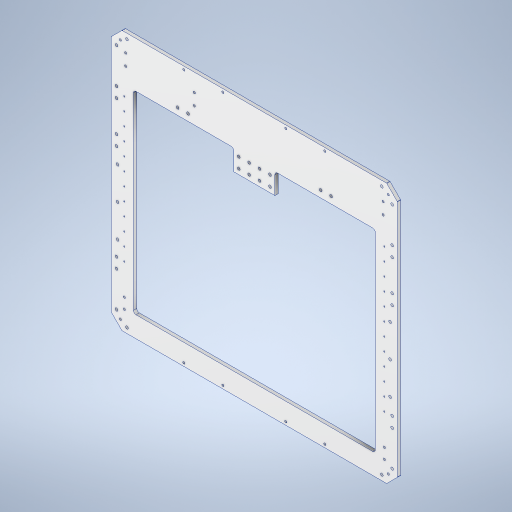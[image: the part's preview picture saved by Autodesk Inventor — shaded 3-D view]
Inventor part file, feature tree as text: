
AUTODESK INVENTOR PART (.ipt)
format: ipt  version: 2024 (Build 280153000, 153)  size: 780,800 bytes
history: native  units: mm
features: sketch x10, hole x6, extrude x4, projected_geometry x4, fillet x3, mirror x2
ambient origin geometry x8: Origin, YZ Plane, XZ Plane, XY Plane, X Axis, Y Axis, Z Axis, Center Point
bodies: Solid1 (feature_tree)
feature tree (29):
  extrude  "Extrusion1"  Depth=500.0mm
  hole  "Hole1"  [1 undecoded]
  extrude  "Extrusion4"  Depth=40.0mm
  extrude  "Extrusion5"  Depth=40.0mm
  hole  "Hole6"  [1 undecoded]
  hole  "Hole7"  [1 undecoded]
  mirror  "Mirror1"
  hole  "Hole8"  [1 undecoded]
  fillet  "Fillet2"  Radius=40.0mm
  fillet  "Fillet3"  Radius=20.0mm
  fillet  "Fillet4"  Radius=40.0mm
  extrude  "Extrusion6"  Depth=40.0mm
  hole  "Hole9"  [1 undecoded]
  hole  "Hole10"  [1 undecoded]
  mirror  "Mirror2"
  sketch  "Sketch1"  dims[d0=550.0mm d1=500.0mm]
  sketch  "Sketch2"  dims[d2=6.35mm d3=0.0mm d4=40.0mm]
  sketch  "Sketch9"  dims[d5=40.0mm d6=40.0mm]
  projected_geometry  "Projected Loop2"
  sketch  "Sketch10"  dims[d7=40.0mm d8=80.0mm]
  sketch  "Sketch11"  dims[d9=40.0mm d10=40.0mm]
  sketch  "Sketch12"  dims[d11=40.0mm d13=40.0mm]
  sketch  "Sketch13"  dims[d14=40.0mm d15=20.0mm d16=40.0mm d17=20.0mm d18=40.0mm]
  sketch  "Sketch14"  dims[d19=40.0mm d20=20.0mm]
  projected_geometry  "Projected Loop3"
  sketch  "Sketch15"  dims[d21=40.0mm d22=20.0mm]
  projected_geometry  "Projected Loop4"
  sketch  "Sketch16"  dims[d23=3.0mm d24=275.0mm d25=20.0mm d26=40.0mm d27=20.0mm d28=40.0mm d29=20.0mm d30=40.0mm d31=20.0mm d32=40.0mm d33=392.0mm d35=10.0mm d36=10.0mm d37=88.0mm d40=88.0mm d42=48.0mm d44=164.0mm d49=10.0mm d51=162.0mm d52=20.0mm d53=20.0mm d54=20.0mm d55=20.0mm d56=20.0mm d57=20.0mm d58=20.0mm d59=20.0mm d60=20.0mm d61=20.0mm d62=20.0mm d63=20.0mm d64=20.0mm d65=20.0mm d66=20.0mm d67=20.0mm d68=20.0mm d69=20.0mm d70=60.0mm d71=20.0mm d72=5.3mm d73=6.0mm d74=4.0mm d75=2.0mm d76=90.0deg d77=8.0mm d78=20.594885mm d79=10.0mm d87=80.0mm d148=465.0mm d150=40.0mm d151=79.2mm d152=40.0mm d153=13.0mm d154=0.0mm d155=0.0mm d156=20.0mm d157=20.0mm d158=0.0mm d159=0.0mm d160=125.0mm d161=2.0mm d162=4.0mm d163=5.3mm d164=6.0mm d165=6.5mm d166=11.0mm d167=90.0deg d168=15.0mm d169=20.594885mm d170=12.0mm d171=300.0mm d172=275.0mm d173=120.0mm d175=25.0mm d176=10.0mm d178=10.0mm d180=25.0mm d181=95.0mm d182=2.459mm d183=6.0mm d184=4.0mm d185=2.0mm d186=90.0deg d187=8.0mm d188=20.594885mm d189=22.0mm d190=34.0mm d191=27.5mm d192=132.0mm d193=20.0mm d194=25.0mm d195=38.0mm d196=4.134mm d197=10.0mm d198=4.0mm d199=2.0mm d200=90.0deg d201=8.0mm d202=20.594885mm d203=5.0mm d204=5.0mm d205=1.0mm d206=10.0mm d207=0.0mm d208=17.5mm d209=17.5mm d210=17.5mm d211=17.5mm d212=4.134mm d213=10.0mm d214=4.0mm d215=2.0mm d216=90.0deg d217=8.0mm d218=20.594885mm d227=75.0mm d228=75.0mm d229=6.0mm d230=196.0mm d231=4.134mm d232=10.0mm d233=9.5mm d234=5.0mm d235=90.0deg d236=8.0mm d237=20.594885mm]
  projected_geometry  "Projected Loop5"
note: 6 required parameter values undecoded (feature->parameter linkage not recoverable at this tier; creation-order binding heuristic only, values carry confidence <= 0.55)
